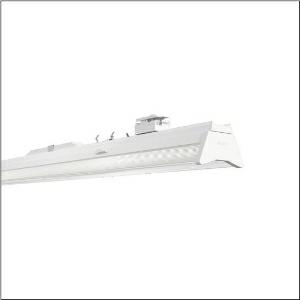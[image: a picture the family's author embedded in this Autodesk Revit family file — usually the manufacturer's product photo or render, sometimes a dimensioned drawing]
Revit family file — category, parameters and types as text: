
# Revit family: licross_11_performance_ho_51tm16cn4exm
name_source: partatom
category: Lighting Fixtures
units: mm (PartAtom-declared; Revit-internal decimal feet)

## family parameters
Cut with Voids When Loaded = No
Host = Face
Light Source = No
Part Type = Normal
Room Calculation Point = No
Round Connector Dimension = Use Diameter
Shared = No

## types (1)
- --- (1 x LED, 14420 lm, 77.6 W, 4000K)
    Apparent Load = 78 VA
    CIE Flux Codes = 63 87 95 78 100
    Color Rendering = 80
    Color Temperature = 4000K
    Default Elevation = 1800 mm
    Description = Licross 11 Performance HO, luminaire insert, of sheet steel, galvanised, coil coated, white, length: 1.500mm, width: 120mm, height: 123mm, LED rated luminous flux: 14.420lm, light colour: 840, SDCM (Standard Deviation of Colour Matching)MacAdam ≤ 2 SDCM (initial), control gear: ON/OFF Multilumen, CLOi, with plug, 3-pole, with phase selection, mains connection: 220..240V, AC, 50/60Hz, start of lifetime: 78W, end of service life: 87W, internal wiring halogen-free, primary light control with lens, of plastic, primary optical cover: cover, of PMMA, light emission: direct/indirect distribution, primary light characteristic: symmetric, protection rating (complete): IP40, insulation class (complete): insulation class I (protective earthing), certification: CE, ENEC, VDE, UKCA, protection symbol: D if used in an environment without relevant dust loads with corresponding accessories, impact resistance: IK06, permissible ambient temperature for indoor applications: -35..+35°C, corresponds to IFS (International Featured Standards) requirements for safety and quality in the food industry, reducing of maximum allowable ambient temperature of 5°C with ceiling mounting, LABS conformity tested according to VDMA 24364:2018-05, The light source and the operating device comply with the requirements of the Ecodesign Regulation (EU) 2019/2020 and are replaceable in accordance with this regulation, packaging unit: 1 piece
    Height = 114 mm
    Lamp = 1 x LED
    Lamp Light Flux = 14420 lm
    Lamp Power = 77.6 W
    Lamp count = 1
    Length = 1500 mm
    Luminous efficacy = 186 lm/W
    Manufacturer = Siteco
    ModVariant = No
    Model = 51TM16CN4EXM
    Mounting Place = Ceiling
    Mounting Type = Pendant
    Number of Poles = 1
    OnlyDefault = Yes
    Power Factor = 1
    Product Name = Licross 11 Performance HO
    Product group = luminaire insert | ceiling pendant
    ProductGroupID = 901
    Protection Class = Protection class I
    Protection Degree = IP 40
    RLX_Detail_Level = 1
    RLX_Emergency_Light_Flux = 0 lm
    RLX_Emergency_Type = 0
    RLX_Emergency_Type_DB = No
    RlxData = <blob elided: 32149 chars, md5=f98dd0e6>
    Socket = socket
    Standby Power = 0 W
    System Light Flux = 14420 lm
    System Power = 78 W
    Type Comments = factory setting: luminous flux: 100 % | (A | C | E) | 181 mA
    Type Image = l_1256138.jpg
    URL = http://relux.com
    VarID = @adj_091541
    Voltage = 0 V
    Weight = 0.00 kg
    Width = 120 mm

## geometry (parser evidence)
native form markers: Blend x4, Sweep x13
no freeform markers — native parametric forms only
